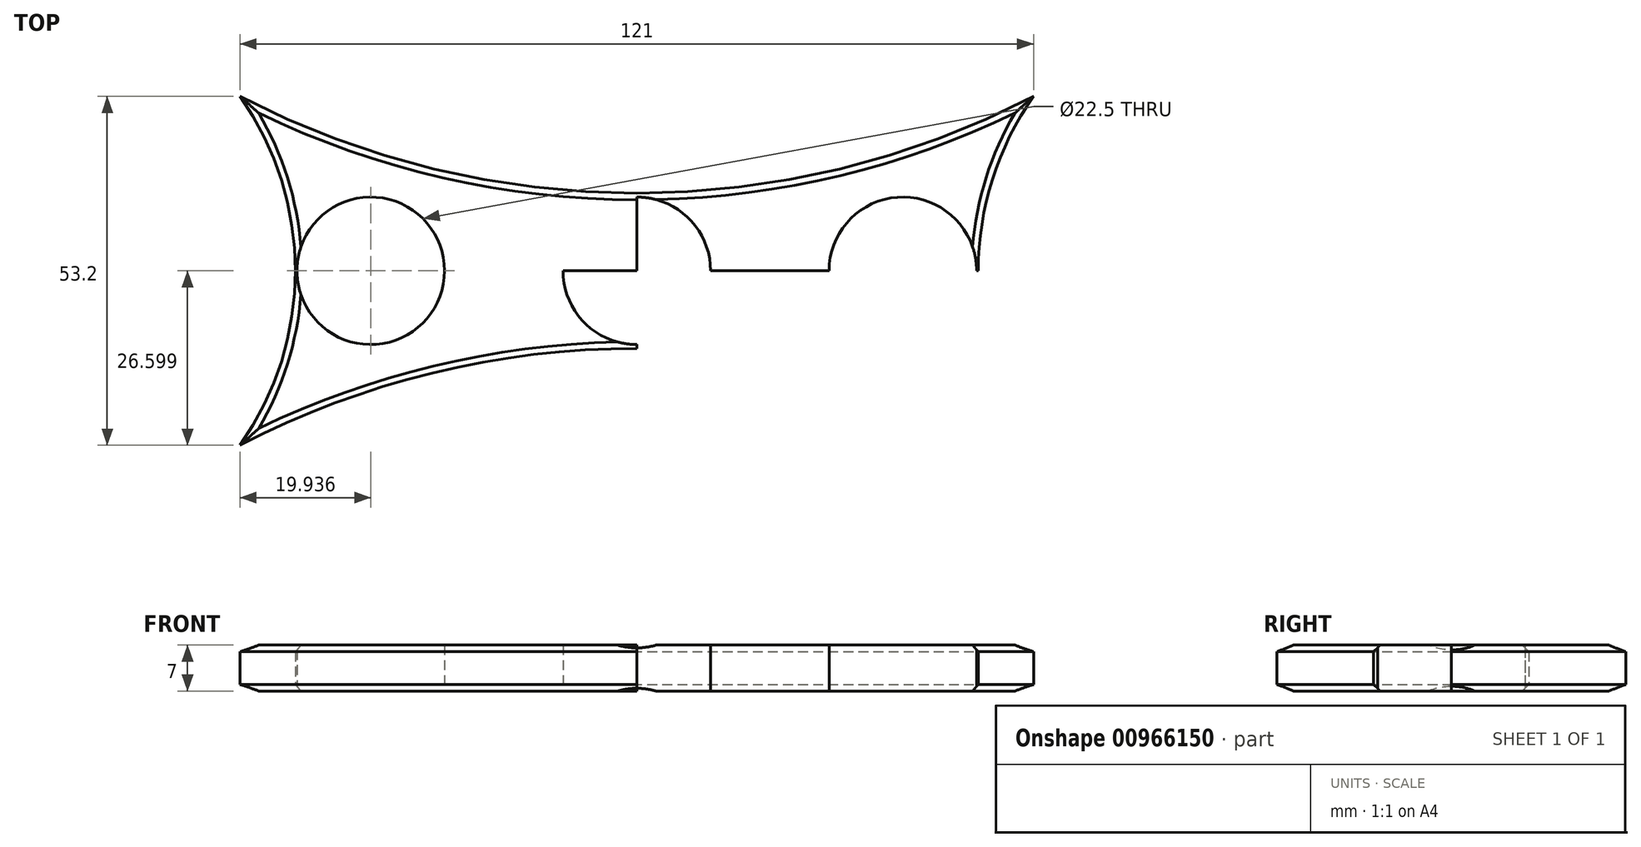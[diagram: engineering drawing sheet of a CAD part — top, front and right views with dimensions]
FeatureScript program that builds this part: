
annotation { "Feature Type Name" : "Feature", "Feature Type Description" : "" }
export const myFeature = defineFeature(function(context is Context, id is Id, definition is map)
    precondition{}
    {
        {
            var Q0;
            Q0=qCreatedBy(makeId("Top.planeOp"),FACE);
            var sketch = newSketch(context, id + "F0", { "sketchPlane" : qUnion([Q0])});
            skLineSegment(sketch, "E0.bottom", {"start": v(-67.47, 29.42) * mm, "end": v(53.53, 29.42) * mm});
            skLineSegment(sketch, "E0.top", {"start": v(-67.47, -23.78) * mm, "end": v(53.53, -23.78) * mm});
            skLineSegment(sketch, "E0.left", {"start": v(-67.47, 29.42) * mm, "end": v(-67.47, -23.78) * mm});
            skLineSegment(sketch, "E0.right", {"start": v(53.53, 29.42) * mm, "end": v(53.53, -23.78) * mm});
            skLineSegment(sketch, "E1", {"start": v(-67.47, 29.42) * mm, "end": v(53.53, -23.78) * mm});
            skCircle(sketch, "E2", {"center": v(-6.97, 2.82) * mm, "radius": 11.25 * mm});
            skCircle(sketch, "E3", {"center": v(-47.53, 2.82) * mm, "radius": 11.25 * mm});
            skLineSegment(sketch, "E4", {"start": v(-6.97, 29.42) * mm, "end": v(-6.97, -23.78) * mm});
            skCircle(sketch, "E5.MirrorC", {"center": v(33.6, 2.82) * mm, "radius": 11.25 * mm});
            skArc(sketch, "E6", {"start": v(-67.47, 29.42) * mm, "mid": v(-6.97, 14.65) * mm, "end": v(53.53, 29.42) * mm});
            skLineSegment(sketch, "E7", {"start": v(-67.47, 2.82) * mm, "end": v(53.53, 2.82) * mm});
            skArc(sketch, "E8.MirrorCS", {"start": v(-67.47, -23.78) * mm, "mid": v(-6.97, -9.02) * mm, "end": v(53.53, -23.78) * mm});
            skArc(sketch, "E9", {"start": v(-67.47, -23.78) * mm, "mid": v(-59.05, 2.82) * mm, "end": v(-67.47, 29.42) * mm});
            skArc(sketch, "E10.MirrorCS", {"start": v(53.53, -23.78) * mm, "mid": v(45.1, 2.82) * mm, "end": v(53.53, 29.42) * mm});
            skSolve(sketch);
        }
        {
            var Q0;
            {var subQ0=sQuery(id+"F0.wireOp",EDGE,"E7");var subQ6=sQuery(id+"F0.wireOp",EDGE,"E2");var subQ12=makeQuery(id+"F0.imprint","INTERSECT",VERTEX,{"disambiguationData":[OD(1.0)],"derivedFrom":[subQ6,subQ0]});Q0=makeQuery(id+"F0.imprint","IMPRINT",FACE,{"disambiguationData":[TD([[makeQuery(id+"F0.imprint","IMPRINT",EDGE,{"disambiguationData":[TD([[subQ12,-1.0]])],"derivedFrom":subQ6}),-1.0]])]});}
            var Q1;
            {var subQ1=sQuery(id+"F0.wireOp",EDGE,"E6");var subQ2=sQuery(id+"F0.wireOp",EDGE,"E1");var subQ4=makeQuery(id+"F0.imprint","INTERSECT",VERTEX,{"derivedFrom":[subQ2,subQ1]});Q1=makeQuery(id+"F0.imprint","IMPRINT",FACE,{"disambiguationData":[TD([[makeQuery(id+"F0.imprint","IMPRINT",EDGE,{"disambiguationData":[TD([[subQ4,-1.0]])],"derivedFrom":subQ2}),-1.0]])]});}
            var Q2;
            {var subQ0=sQuery(id+"F0.wireOp",EDGE,"E6");var subQ1=sQuery(id+"F0.wireOp",EDGE,"E1");var subQ2=makeQuery(id+"F0.imprint","INTERSECT",VERTEX,{"derivedFrom":[subQ1,subQ0]});Q2=makeQuery(id+"F0.imprint","IMPRINT",FACE,{"disambiguationData":[TD([[makeQuery(id+"F0.imprint","IMPRINT",EDGE,{"disambiguationData":[TD([[subQ2,-1.0]])],"derivedFrom":subQ1}),1.0]])]});}
            var Q3;
            {var subQ0=sQuery(id+"F0.wireOp",EDGE,"E2");var subQ1=sQuery(id+"F0.wireOp",EDGE,"E1");var subQ2=makeQuery(id+"F0.imprint","INTERSECT",VERTEX,{"disambiguationData":[OD(1.0)],"derivedFrom":[subQ1,subQ0]});Q3=makeQuery(id+"F0.imprint","IMPRINT",FACE,{"disambiguationData":[TD([[makeQuery(id+"F0.imprint","IMPRINT",EDGE,{"disambiguationData":[TD([[subQ2,-1.0]])],"derivedFrom":subQ1}),-1.0]])]});}
            var Q4;
            {var subQ1=sQuery(id+"F0.wireOp",EDGE,"E2");var subQ6=sQuery(id+"F0.wireOp",EDGE,"E1");var subQ7=makeQuery(id+"F0.imprint","INTERSECT",VERTEX,{"disambiguationData":[OD(1.0)],"derivedFrom":[subQ6,subQ1]});Q4=makeQuery(id+"F0.imprint","IMPRINT",FACE,{"disambiguationData":[TD([[makeQuery(id+"F0.imprint","IMPRINT",EDGE,{"disambiguationData":[TD([[subQ7,-1.0]])],"derivedFrom":subQ6}),1.0]])]});}
            var Q5;
            {var subQ3=sQuery(id+"F0.wireOp",EDGE,"E4");var subQ9=sQuery(id+"F0.wireOp",EDGE,"E2");var subQ11=makeQuery(id+"F0.imprint","INTERSECT",VERTEX,{"disambiguationData":[OD(0.0)],"derivedFrom":[subQ9,subQ3]});Q5=makeQuery(id+"F0.imprint","IMPRINT",FACE,{"disambiguationData":[TD([[makeQuery(id+"F0.imprint","IMPRINT",EDGE,{"disambiguationData":[TD([[subQ11,1.0]])],"derivedFrom":subQ9}),-1.0]])]});}
            extrude(context, id + "F1", {"entities" : qUnion([Q0, Q1, Q2, Q3, Q4, Q5]), "depth" : 7 * mm, "offsetDistance" : 25 * mm});
        }
        {
            var Q0;
            Q0=makeQuery(id+"F1.opExtrude","CAP_EDGE",EDGE,{"disambiguationData":[OSD([sQuery(id+"F0.wireOp",EDGE,"E8.MirrorCS")])],"isStart":false});
            var Q1;
            Q1=makeQuery(id+"F1.opExtrude","CAP_EDGE",EDGE,{"disambiguationData":[OSD([sQuery(id+"F0.wireOp",EDGE,"E6")])],"isStart":false});
            var Q2;
            Q2=makeQuery(id+"F1.opExtrude","CAP_EDGE",EDGE,{"disambiguationData":[OSD([sQuery(id+"F0.wireOp",EDGE,"E9")])],"isStart":false});
            var Q3;
            Q3=makeQuery(id+"F1.opExtrude","CAP_EDGE",EDGE,{"disambiguationData":[OSD([sQuery(id+"F0.wireOp",EDGE,"E9")])],"isStart":true});
            var Q4;
            Q4=makeQuery(id+"F1.opExtrude","CAP_EDGE",EDGE,{"disambiguationData":[OSD([sQuery(id+"F0.wireOp",EDGE,"E6")])],"isStart":true});
            var Q5;
            Q5=makeQuery(id+"F1.opExtrude","CAP_EDGE",EDGE,{"disambiguationData":[OSD([sQuery(id+"F0.wireOp",EDGE,"E10.MirrorCS")])],"isStart":true});
            var Q6;
            Q6=makeQuery(id+"F1.opExtrude","CAP_EDGE",EDGE,{"disambiguationData":[OSD([sQuery(id+"F0.wireOp",EDGE,"E10.MirrorCS")])],"isStart":false});
            var Q7;
            Q7=makeQuery(id+"F1.opExtrude","CAP_EDGE",EDGE,{"disambiguationData":[OSD([sQuery(id+"F0.wireOp",EDGE,"E8.MirrorCS")])],"isStart":true});
            chamfer(context, id + "F2", {"entities" : qUnion([Q0, Q1, Q2, Q3, Q4, Q5, Q6, Q7]), "width" : 1 * mm, "tangentPropagation" : true});
        }
    });
